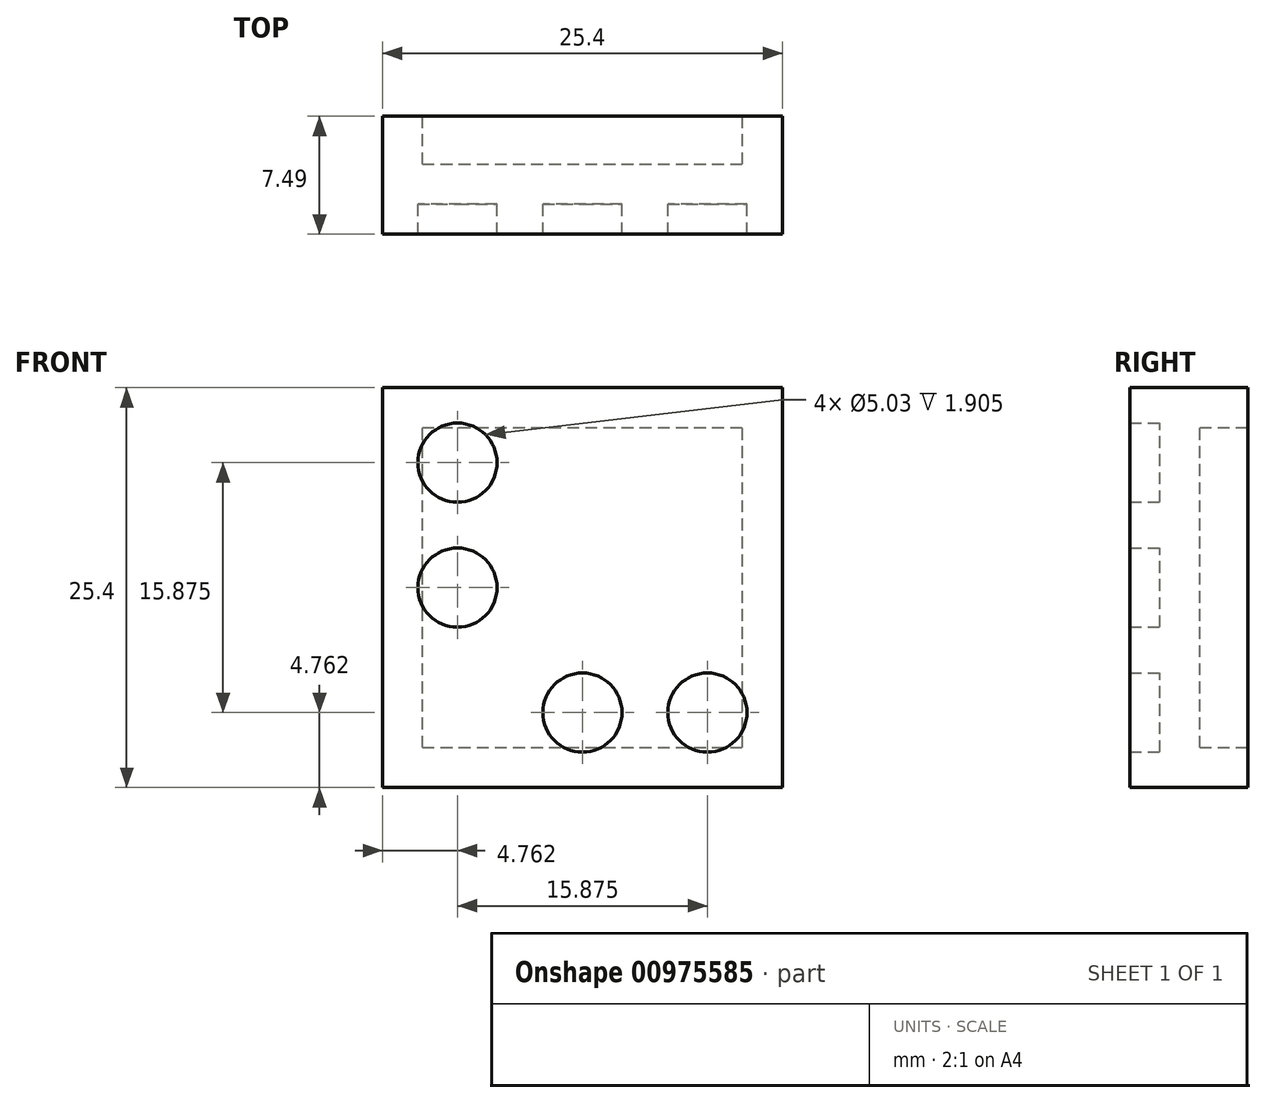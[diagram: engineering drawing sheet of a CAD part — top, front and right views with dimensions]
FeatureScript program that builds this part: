
annotation { "Feature Type Name" : "Feature", "Feature Type Description" : "" }
export const myFeature = defineFeature(function(context is Context, id is Id, definition is map)
    precondition{}
    {
        {
            var Q0;
            Q0=qCreatedBy(makeId("Front.planeOp"),FACE);
            var sketch = newSketch(context, id + "F0", { "sketchPlane" : qUnion([Q0])});
            skLineSegment(sketch, "E0.bottom", {"start": v(-12.7, -12.7) * mm, "end": v(12.7, -12.7) * mm});
            skLineSegment(sketch, "E0.top", {"start": v(-12.7, 12.7) * mm, "end": v(12.7, 12.7) * mm});
            skLineSegment(sketch, "E0.left", {"start": v(-12.7, -12.7) * mm, "end": v(-12.7, 12.7) * mm});
            skLineSegment(sketch, "E0.right", {"start": v(12.7, -12.7) * mm, "end": v(12.7, 12.7) * mm});
            skPoint(sketch, "E0.middle", {"position": v(0, 0) * mm});
            skSolve(sketch);
        }
        {
            var Q0;
            Q0=makeQuery(id+"F0.imprint","IMPRINT",FACE,{"disambiguationData":[TD([[makeQuery(id+"F0.imprint","IMPRINT",EDGE,{"derivedFrom":sQuery(id+"F0.wireOp",EDGE,"E0.bottom")}),1.0]])]});
            extrude(context, id + "F1", {"entities" : qUnion([Q0]), "depth" : 5.6 * mm, "offsetDistance" : 25.4 * mm});
        }
        {
            var Q0;
            Q0=makeQuery(id+"F1.opExtrude","CAP_FACE",FACE,{"disambiguationData":[OSD([sQuery(id+"F0.wireOp",EDGE,"E0.bottom"),sQuery(id+"F0.wireOp",EDGE,"E0.top"),sQuery(id+"F0.wireOp",EDGE,"E0.left"),sQuery(id+"F0.wireOp",EDGE,"E0.right")])],"isStart":false});
            var sketch = newSketch(context, id + "F2", { "sketchPlane" : qUnion([Q0])});
            skCircle(sketch, "E1", {"center": v(0, 0) * mm, "radius": 2.51 * mm});
            skCircle(sketch, "E2.1.0.0", {"center": v(7.94, 0) * mm, "radius": 2.51 * mm});
            skLineSegment(sketch, "E2.direction1", {"start": v(0, 0) * mm, "end": v(7.94, 0) * mm, "construction": true});
            skLineSegment(sketch, "E3", {"start": v(0, 12.7) * mm, "end": v(0, -12.7) * mm, "construction": true});
            skLineSegment(sketch, "E4", {"start": v(-12.7, 0) * mm, "end": v(12.7, 0) * mm, "construction": true});
            skCircle(sketch, "E5.1.0.0", {"center": v(0, 7.94) * mm, "radius": 2.51 * mm});
            skLineSegment(sketch, "E5.direction1", {"start": v(0, 0) * mm, "end": v(0, 7.94) * mm, "construction": true});
            skCircle(sketch, "E6.MirrorC", {"center": v(-7.94, 0) * mm, "radius": 2.51 * mm});
            skCircle(sketch, "E7.MirrorC", {"center": v(0, -7.94) * mm, "radius": 2.51 * mm});
            skCircle(sketch, "E8.1.0.0", {"center": v(-7.94, 7.94) * mm, "radius": 2.51 * mm});
            skLineSegment(sketch, "E8.direction1", {"start": v(-7.94, 0) * mm, "end": v(-7.94, 7.94) * mm, "construction": true});
            skCircle(sketch, "E9.MirrorC", {"center": v(-7.94, -7.94) * mm, "radius": 2.51 * mm});
            skCircle(sketch, "E10.MirrorC", {"center": v(7.94, -7.94) * mm, "radius": 2.51 * mm});
            skCircle(sketch, "E11.MirrorC", {"center": v(7.94, 7.94) * mm, "radius": 2.51 * mm});
            skSolve(sketch);
        }
        {
            var Q0;
            Q0=makeQuery(id+"F1.opExtrude","CAP_FACE",FACE,{"disambiguationData":[OSD([sQuery(id+"F0.wireOp",EDGE,"E0.bottom"),sQuery(id+"F0.wireOp",EDGE,"E0.top"),sQuery(id+"F0.wireOp",EDGE,"E0.left"),sQuery(id+"F0.wireOp",EDGE,"E0.right")])],"isStart":true});
            shell(context, id + "F3", {"entities" : qUnion([Q0]), "thickness" : 2.54 * mm});
        }
        {
            var Q0;
            Q0=makeQuery(id+"F2.imprint","IMPRINT",FACE,{"disambiguationData":[TD([[makeQuery(id+"F2.imprint","IMPRINT",EDGE,{"derivedFrom":sQuery(id+"F2.wireOp",EDGE,"E8.1.0.0")}),-1.0]])]});
            var Q1;
            Q1=makeQuery(id+"F2.imprint","IMPRINT",FACE,{"disambiguationData":[TD([[makeQuery(id+"F2.imprint","IMPRINT",EDGE,{"derivedFrom":sQuery(id+"F2.wireOp",EDGE,"E5.1.0.0")}),1.0]])]});
            var Q2;
            Q2=makeQuery(id+"F2.imprint","IMPRINT",FACE,{"disambiguationData":[TD([[makeQuery(id+"F2.imprint","IMPRINT",EDGE,{"derivedFrom":sQuery(id+"F2.wireOp",EDGE,"E11.MirrorC")}),1.0]])]});
            var Q3;
            Q3=makeQuery(id+"F2.imprint","IMPRINT",FACE,{"disambiguationData":[TD([[makeQuery(id+"F2.imprint","IMPRINT",EDGE,{"derivedFrom":sQuery(id+"F2.wireOp",EDGE,"E2.1.0.0")}),1.0]])]});
            var Q4;
            Q4=makeQuery(id+"F2.imprint","IMPRINT",FACE,{"disambiguationData":[TD([[makeQuery(id+"F2.imprint","IMPRINT",EDGE,{"derivedFrom":sQuery(id+"F2.wireOp",EDGE,"E1")}),1.0]])]});
            var Q5;
            Q5=makeQuery(id+"F2.imprint","IMPRINT",FACE,{"disambiguationData":[TD([[makeQuery(id+"F2.imprint","IMPRINT",EDGE,{"derivedFrom":sQuery(id+"F2.wireOp",EDGE,"E6.MirrorC")}),-1.0]])]});
            var Q6;
            Q6=makeQuery(id+"F2.imprint","IMPRINT",FACE,{"disambiguationData":[TD([[makeQuery(id+"F2.imprint","IMPRINT",EDGE,{"derivedFrom":sQuery(id+"F2.wireOp",EDGE,"E9.MirrorC")}),1.0]])]});
            var Q7;
            Q7=makeQuery(id+"F2.imprint","IMPRINT",FACE,{"disambiguationData":[TD([[makeQuery(id+"F2.imprint","IMPRINT",EDGE,{"derivedFrom":sQuery(id+"F2.wireOp",EDGE,"E7.MirrorC")}),-1.0]])]});
            var Q8;
            Q8=makeQuery(id+"F2.imprint","IMPRINT",FACE,{"disambiguationData":[TD([[makeQuery(id+"F2.imprint","IMPRINT",EDGE,{"derivedFrom":sQuery(id+"F2.wireOp",EDGE,"E10.MirrorC")}),-1.0]])]});
            extrude(context, id + "F4", {"entities" : qUnion([Q0, Q1, Q2, Q3, Q4, Q5, Q6, Q7, Q8]), "operationType" : NewBodyOperationType.ADD, "depth" : 1.9 * mm, "offsetDistance" : 25.4 * mm});
        }
    });
